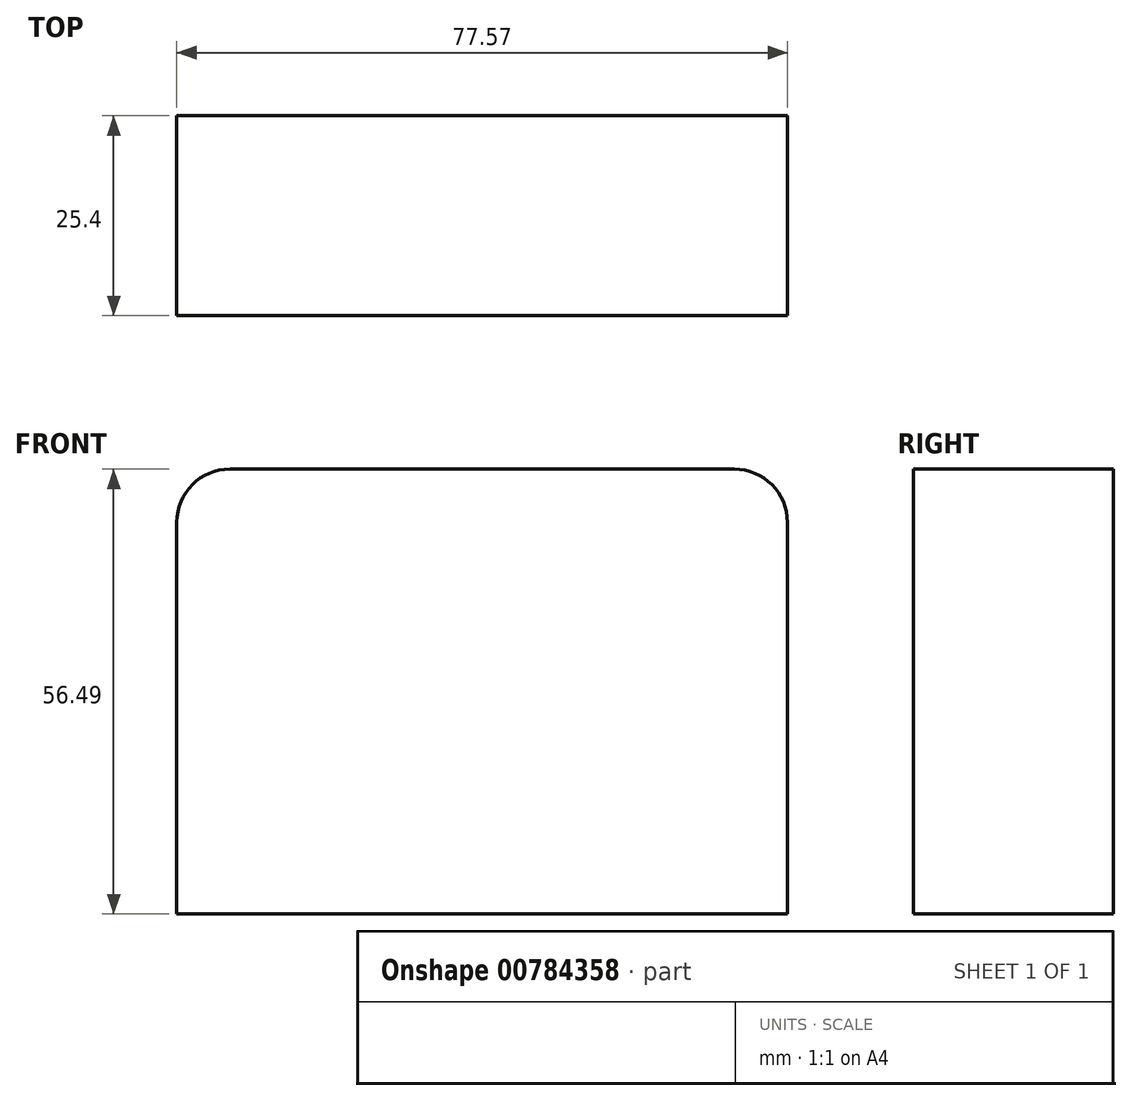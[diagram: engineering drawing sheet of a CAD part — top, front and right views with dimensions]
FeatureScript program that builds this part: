
annotation { "Feature Type Name" : "Feature", "Feature Type Description" : "" }
export const myFeature = defineFeature(function(context is Context, id is Id, definition is map)
    precondition{}
    {
        {
            var Q0;
            Q0=qCreatedBy(makeId("Front.planeOp"),FACE);
            var sketch = newSketch(context, id + "F0", { "sketchPlane" : qUnion([Q0])});
            skLineSegment(sketch, "E0.bottom", {"start": v(-34.05, 27.94) * mm, "end": v(43.52, 27.94) * mm});
            skLineSegment(sketch, "E0.top", {"start": v(-34.05, -28.55) * mm, "end": v(43.52, -28.55) * mm});
            skLineSegment(sketch, "E0.left", {"start": v(-34.05, 27.94) * mm, "end": v(-34.05, -28.55) * mm});
            skLineSegment(sketch, "E0.right", {"start": v(43.52, 27.94) * mm, "end": v(43.52, -28.55) * mm});
            skSolve(sketch);
        }
        {
            var Q0;
            Q0=makeQuery(id+"F0.imprint","IMPRINT",FACE,{"disambiguationData":[TD([[makeQuery(id+"F0.imprint","IMPRINT",EDGE,{"derivedFrom":sQuery(id+"F0.wireOp",EDGE,"E0.bottom")}),-1.0]])]});
            extrude(context, id + "F1", {"entities" : qUnion([Q0]), "depth" : 25.4 * mm, "offsetDistance" : 25.4 * mm});
        }
        {
            var Q0;
            Q0=makeQuery(id+"F1.opExtrude","CAP_FACE",FACE,{"disambiguationData":[OSD([sQuery(id+"F0.wireOp",EDGE,"E0.bottom"),sQuery(id+"F0.wireOp",EDGE,"E0.top"),sQuery(id+"F0.wireOp",EDGE,"E0.left"),sQuery(id+"F0.wireOp",EDGE,"E0.right")])],"isStart":false});
            var sketch = newSketch(context, id + "F2", { "sketchPlane" : qUnion([Q0])});
            skCircle(sketch, "E1", {"center": v(0, 0) * mm, "radius": 8.92 * mm});
            skSolve(sketch);
        }
        {
            var Q0;
            Q0=makeQuery(id+"F2.imprint","IMPRINT",FACE,{"disambiguationData":[TD([[makeQuery(id+"F2.imprint","IMPRINT",EDGE,{"derivedFrom":sQuery(id+"F2.wireOp",EDGE,"E1")}),1.0]])]});
            extrude(context, id + "F3", {"entities" : qUnion([Q0]), "operationType" : NewBodyOperationType.ADD, "depth" : -25.4 * mm, "offsetDistance" : 25.4 * mm});
        }
        {
            var Q0;
            Q0=makeQuery(id+"F1.opExtrude","SWEPT_EDGE",EDGE,{"disambiguationData":[OSD([sQuery(id+"F0.wireOp",EDGE,"E0.bottom"),sQuery(id+"F0.wireOp",EDGE,"E0.left")])]});
            fillet(context, id + "F4", {"entities" : qUnion([Q0]), "radius" : 6.75 * mm, "tangentPropagation" : true, "allowEdgeOverflow" : false});
        }
        {
            var Q0;
            Q0=makeQuery(id+"F1.opExtrude","SWEPT_EDGE",EDGE,{"disambiguationData":[OSD([sQuery(id+"F0.wireOp",EDGE,"E0.bottom"),sQuery(id+"F0.wireOp",EDGE,"E0.right")])]});
            fillet(context, id + "F5", {"entities" : qUnion([Q0]), "radius" : 6.76 * mm, "tangentPropagation" : true, "allowEdgeOverflow" : false});
        }
    });
